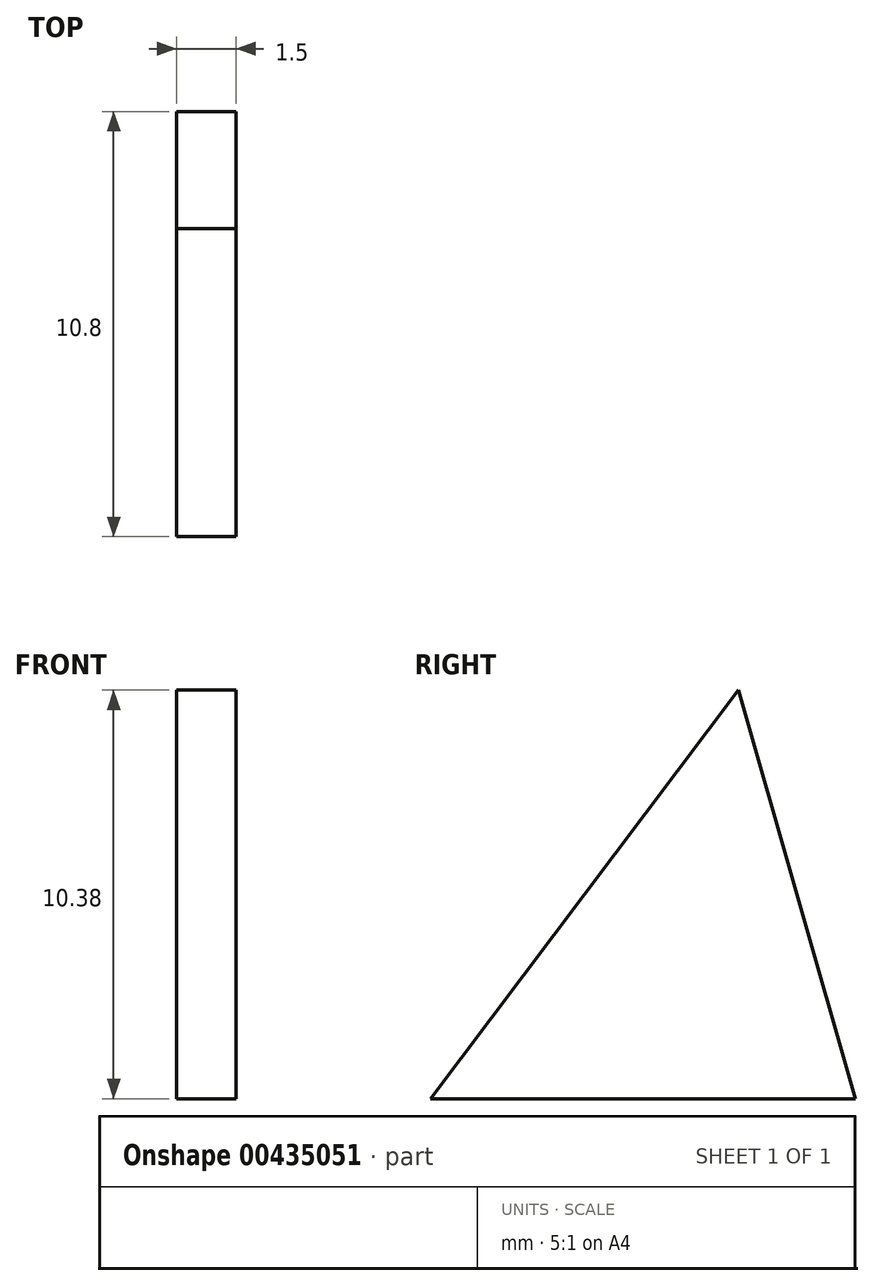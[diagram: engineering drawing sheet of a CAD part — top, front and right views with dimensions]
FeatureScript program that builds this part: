
annotation { "Feature Type Name" : "Feature", "Feature Type Description" : "" }
export const myFeature = defineFeature(function(context is Context, id is Id, definition is map)
    precondition{}
    {
        {
            var Q0;
            Q0=qCreatedBy(makeId("Right.planeOp"),FACE);
            var sketch = newSketch(context, id + "F0", { "sketchPlane" : qUnion([Q0])});
            skLineSegment(sketch, "E0", {"start": v(0, 0) * mm, "end": v(7.82, 10.38) * mm});
            skLineSegment(sketch, "E1", {"start": v(7.82, 10.38) * mm, "end": v(10.8, 0) * mm});
            skLineSegment(sketch, "E2", {"start": v(10.8, 0) * mm, "end": v(0, 0) * mm});
            skSolve(sketch);
        }
        {
            var Q0;
            Q0 = qSketchRegion(id + "F0", true);
            extrude(context, id + "F1", {"entities" : qUnion([Q0]), "depth" : 1.5 * mm});
        }
    });
